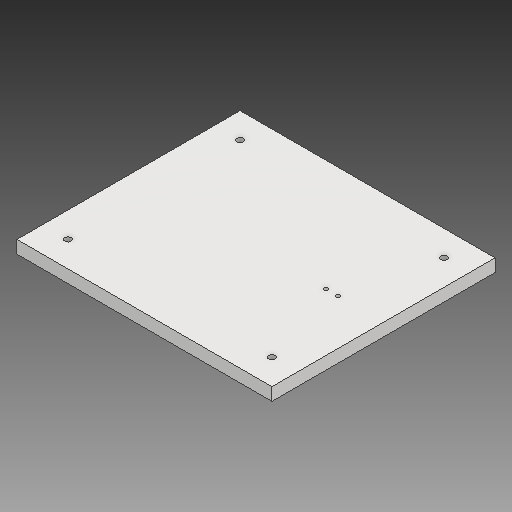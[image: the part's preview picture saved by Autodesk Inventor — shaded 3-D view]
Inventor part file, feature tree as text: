
AUTODESK INVENTOR PART (.ipt)
format: ipt  version: 2018.1 (Build 221171000, 171)  size: 126,464 bytes
history: native  units: mm
features: extrude x4, sketch x4, other x1
ambient origin geometry x8: Origin, YZ Plane, XZ Plane, XY Plane, X Axis, Y Axis, Z Axis, Center Point
bodies: Solid1 (feature_tree)
feature tree (9):
  parser-record x1  (decoder bookkeeping rows leaked as tree rows — omitted from the tree; the rows remain in map.json)
  extrude  "Extrusion1"  Depth=350.0mm
  extrude  "Extrusion7"  Depth=20.0mm
  extrude  "Extrusion8"  Depth=20.0mm
  extrude  "Extrusion9"  Depth=10.0mm
  sketch  "Sketch1"  dims[d0=400.0mm d1=350.0mm]
  sketch  "Sketch7"  dims[d2=20.0mm d3=0.0mm d20=20.0mm]
  sketch  "Sketch8"  dims[d21=0.0mm d22=20.0mm]
  sketch  "Sketch9"  dims[d23=0.0mm d24=10.0mm d25=10.0mm d26=6.0mm d27=0.0mm]
note: 1 file-system path scrubbed to <path> (originals preserved in map.json)
